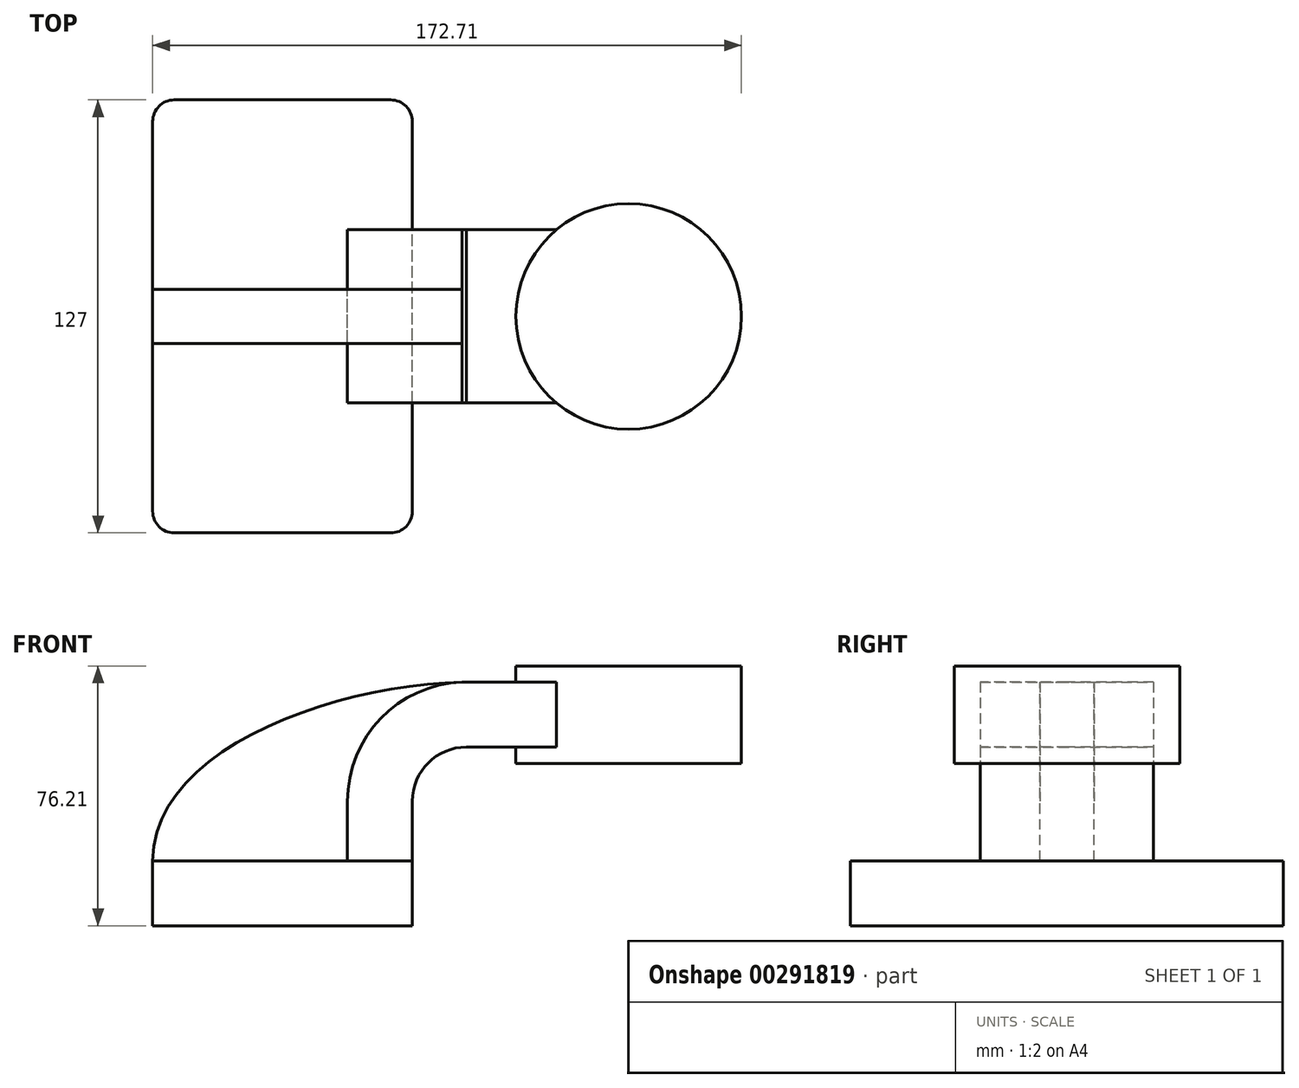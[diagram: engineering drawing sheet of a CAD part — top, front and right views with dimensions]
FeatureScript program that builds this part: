
annotation { "Feature Type Name" : "Feature", "Feature Type Description" : "" }
export const myFeature = defineFeature(function(context is Context, id is Id, definition is map)
    precondition{}
    {
        {
            var Q0;
            Q0=qCreatedBy(makeId("Front.planeOp"),FACE);
            var sketch = newSketch(context, id + "F0", { "sketchPlane" : qUnion([Q0])});
            skLineSegment(sketch, "E0.bottom", {"start": v(-38.1, -9.53) * mm, "end": v(38.1, -9.53) * mm});
            skLineSegment(sketch, "E0.top", {"start": v(-38.1, 9.52) * mm, "end": v(38.1, 9.52) * mm});
            skLineSegment(sketch, "E0.left", {"start": v(-38.1, -9.53) * mm, "end": v(-38.1, 9.52) * mm});
            skLineSegment(sketch, "E0.right", {"start": v(38.1, -9.52) * mm, "end": v(38.1, 9.53) * mm});
            skPoint(sketch, "E0.middle", {"position": v(0, 0) * mm});
            skLineSegment(sketch, "E1.bottom", {"start": v(83.81, 38.1) * mm, "end": v(134.61, 38.1) * mm});
            skLineSegment(sketch, "E1.top", {"start": v(83.81, 66.67) * mm, "end": v(134.61, 66.67) * mm});
            skLineSegment(sketch, "E1.left", {"start": v(83.81, 38.1) * mm, "end": v(83.81, 66.67) * mm});
            skLineSegment(sketch, "E1.right", {"start": v(134.61, 38.1) * mm, "end": v(134.61, 66.67) * mm});
            skPoint(sketch, "E1.middle", {"position": v(109.21, 52.39) * mm});
            skLineSegment(sketch, "E2", {"start": v(38.1, 9.52) * mm, "end": v(38.1, 27) * mm});
            skArc(sketch, "E3", {"start": v(38.1, 27) * mm, "mid": v(42.75, 38.23) * mm, "end": v(53.97, 42.88) * mm});
            skLineSegment(sketch, "E4", {"start": v(53.97, 42.88) * mm, "end": v(101.53, 42.88) * mm});
            skLineSegment(sketch, "E5.0", {"start": v(53.97, 61.93) * mm, "end": v(101.53, 61.93) * mm});
            skArc(sketch, "E5.1", {"start": v(19.05, 27) * mm, "mid": v(29.28, 51.7) * mm, "end": v(53.97, 61.93) * mm});
            skLineSegment(sketch, "E5.2", {"start": v(19.05, 9.52) * mm, "end": v(19.05, 27) * mm});
            skLineSegment(sketch, "E6", {"start": v(101.53, 38.1) * mm, "end": v(101.53, 66.67) * mm});
            skFitSpline(sketch, "E7", {"points": [v(-38.1, 9.53) * mm, v(53.97, 61.93) * mm], "startDerivative": vector(1.14, 100.14) * mm, "endDerivative": vector(113.88, 1.49) * mm});
            skSolve(sketch);
        }
        {
            var Q0;
            Q0=makeQuery(id+"F0.imprint","IMPRINT",FACE,{"disambiguationData":[TD([[makeQuery(id+"F0.imprint","IMPRINT",EDGE,{"derivedFrom":sQuery(id+"F0.wireOp",EDGE,"E0.bottom")}),1.0]])]});
            extrude(context, id + "F1", {"entities" : qUnion([Q0]), "endBound" : BoundingType.SYMMETRIC, "depth" : 127 * mm});
        }
        {
            var Q0;
            {var subQ0=sQuery(id+"F0.wireOp",EDGE,"E4");var subQ1=sQuery(id+"F0.wireOp",EDGE,"E1.left");var subQ2=makeQuery(id+"F0.imprint","INTERSECT",VERTEX,{"derivedFrom":[subQ1,subQ0]});Q0=makeQuery(id+"F0.imprint","IMPRINT",FACE,{"disambiguationData":[TD([[makeQuery(id+"F0.imprint","IMPRINT",EDGE,{"disambiguationData":[TD([[subQ2,-1.0]])],"derivedFrom":subQ1}),-1.0]])]});}
            var Q1;
            {var subQ1=sQuery(id+"F0.wireOp",EDGE,"E2");Q1=makeQuery(id+"F0.imprint","IMPRINT",FACE,{"disambiguationData":[TD([[makeQuery(id+"F0.imprint","IMPRINT",EDGE,{"derivedFrom":subQ1}),1.0]])]});}
            extrude(context, id + "F2", {"entities" : qUnion([Q0, Q1]), "endBound" : BoundingType.SYMMETRIC, "depth" : 50.8 * mm});
        }
        {
            var Q0;
            {var subQ3=sQuery(id+"F0.wireOp",EDGE,"E5.2");Q0=makeQuery(id+"F0.imprint","IMPRINT",FACE,{"disambiguationData":[TD([[makeQuery(id+"F0.imprint","IMPRINT",EDGE,{"derivedFrom":subQ3}),1.0]])]});}
            extrude(context, id + "F3", {"entities" : qUnion([Q0]), "endBound" : BoundingType.SYMMETRIC, "depth" : 15.88 * mm});
        }
        {
            var Q0;
            {var subQ4=sQuery(id+"F0.wireOp",EDGE,"E1.right");Q0=makeQuery(id+"F0.imprint","IMPRINT",FACE,{"disambiguationData":[TD([[makeQuery(id+"F0.imprint","IMPRINT",EDGE,{"derivedFrom":subQ4}),1.0]])]});}
            var Q1;
            Q1=sQuery(id+"F0.wireOp",EDGE,"E6");
            revolve(context, id + "F4", {"operationType" : NewBodyOperationType.ADD, "entities" : qUnion([Q0]), "axis" : qUnion([Q1]), "revolveType" : RevolveType.FULL});
        }
        {
            var Q0;
            Q0=makeQuery(id+"F1.opExtrude","CAP_EDGE",EDGE,{"disambiguationData":[OSD([sQuery(id+"F0.wireOp",EDGE,"E0.left")])],"isStart":false});
            var Q1;
            Q1=makeQuery(id+"F1.opExtrude","CAP_EDGE",EDGE,{"disambiguationData":[OSD([sQuery(id+"F0.wireOp",EDGE,"E0.right")])],"isStart":false});
            var Q2;
            Q2=makeQuery(id+"F1.opExtrude","CAP_EDGE",EDGE,{"disambiguationData":[OSD([sQuery(id+"F0.wireOp",EDGE,"E0.left")])],"isStart":true});
            var Q3;
            Q3=makeQuery(id+"F1.opExtrude","CAP_EDGE",EDGE,{"disambiguationData":[OSD([sQuery(id+"F0.wireOp",EDGE,"E0.right")])],"isStart":true});
            fillet(context, id + "F5", {"entities" : qUnion([Q0, Q1, Q2, Q3]), "radius" : 6.35 * mm, "tangentPropagation" : true, "allowEdgeOverflow" : false});
        }
    });
